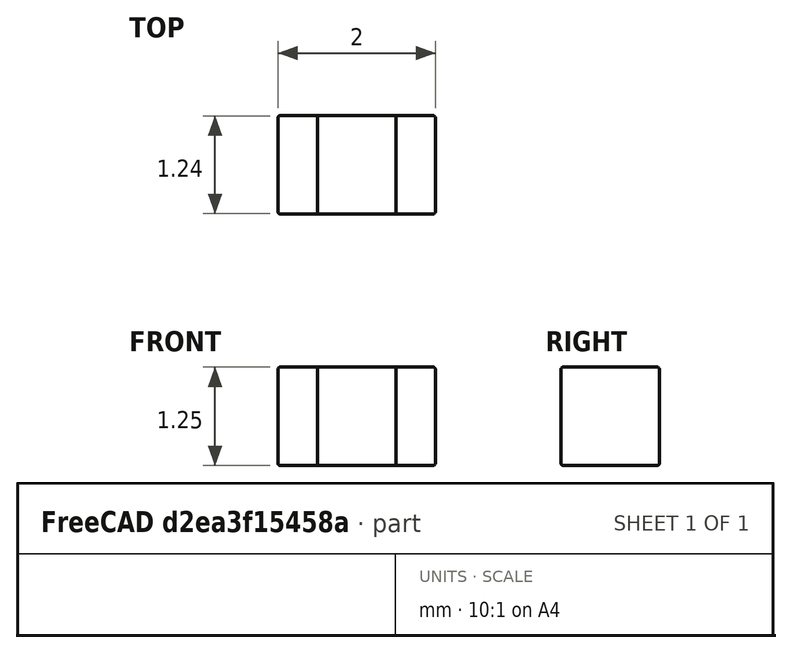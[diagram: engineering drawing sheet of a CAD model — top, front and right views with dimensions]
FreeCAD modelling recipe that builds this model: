
FCSTD DOCUMENT  (FreeCAD 0.16R6703 (Git))
Label: L_0805
License: All rights reserved
LicenseURL: http://en.wikipedia.org/wiki/All_rights_reserved
objects: Part::FeaturePython×4, Part::Box×2, Part::Fillet×2, Part::Mirroring×1, App::DocumentObjectGroup×1
note: 9 computed .brp shape members not serialized (recipe doc carries the construction recipe); baked Part::Feature solids carry a one-line shape summary decoded from their .brp

FEATURE [Part::Box] Box  label="Cube"
  Height = 1.25
  Length = 1
  Placement = pos=(-0.5,-0.38,0.02) rot=(0,0,1;0rad)
  Width = 1.25
FEATURE [Part::Fillet] Fillet  label="body-src"
  Base = -> Box
  Edges = 4 edges r=0.04: [Edge9,Edge10,Edge11,Edge12]
FEATURE [Part::Box] Box001  label="side-src"
  Height = 1.25
  Length = 0.5
  Placement = pos=(-0.8,-0.4,0) rot=(0,0,1;0rad)
  Width = 1.25
FEATURE [Part::Fillet] Fillet001  label="left-side-src"
  Base = -> Box001
  Edges = 8 edges r=0.03: [Edge1,Edge2,Edge3,Edge4,Edge9,Edge10,Edge11,Edge12]
FEATURE [Part::FeaturePython] Clone001  label="left-side-2"  # Draft clone (typed FeaturePython)
  Objects = -> [Fillet001]
  Scale = (1,1,1)
FEATURE [Part::Mirroring] Part__Mirroring  label="right-side-src"
  Base = (0,0,0)
  Normal = (1,0,0)
  Source = -> Clone001
FEATURE [App::DocumentObjectGroup] Group  label="src"
  Group = -> [Fillet,Box001,Fillet001,Part__Mirroring]
FEATURE [Part::FeaturePython] Clone  label="body"  # Draft clone (typed FeaturePython)
  Objects = -> [Fillet]
  Placement = pos=(0,-0.245,-0.02) rot=(0,0,1;0rad)
  Scale = (1,1,1)
FEATURE [Part::FeaturePython] Clone003  label="right-side"  # Draft clone (typed FeaturePython)
  Objects = -> [Part__Mirroring]
  Placement = pos=(0.2,-0.225,0) rot=(0,0,1;0rad)
  Scale = (1,1,1)
FEATURE [Part::FeaturePython] Clone004  label="left-side"  # Draft clone (typed FeaturePython)
  Objects = -> [Clone001]
  Placement = pos=(-0.2,-0.225,0) rot=(0,0,1;0rad)
  Scale = (1,1,1)
